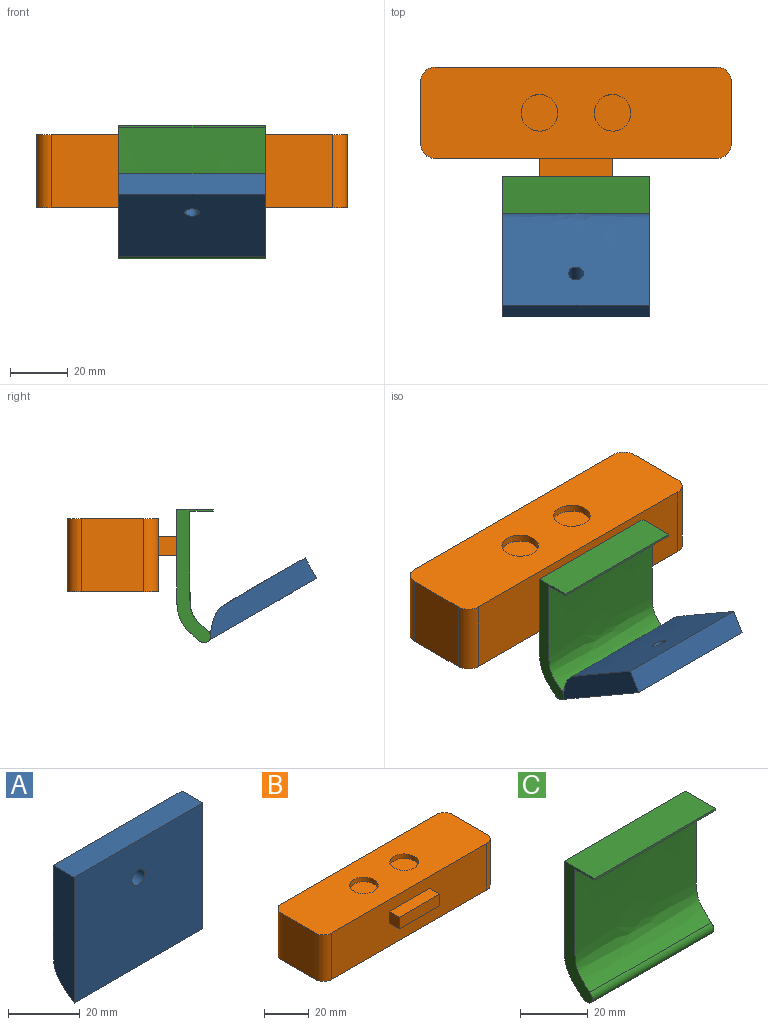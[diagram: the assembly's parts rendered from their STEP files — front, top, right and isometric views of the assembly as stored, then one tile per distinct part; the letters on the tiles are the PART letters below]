
ASSEMBLY  parts=3 mates=2
PART A: 6 faces, bbox 50.8x8.3x43 mm
  f0: extruded ~50.8x42.97mm, area 2327.7mm2, adj f1,f2,f3,f4,f5
  f1: plane 50.8x8.18mm, normal (0,0,1), area 415.3mm2, adj f0,f2,f3,f4
  f2: plane 50.8x42.97mm, normal (0,-1,0), area 2162.3mm2, adj f0,f1,f3,f4,f5
  f3: plane 42.97x8.26mm, normal (1,0,0), area 321.8mm2, adj f0,f1,f2
  f4: plane 42.97x8.26mm, normal (-1,0,0), area 321.8mm2, adj f0,f1,f2
  f5: cylinder r=2.55mm len=8.21mm, axis (0,-1,0), area 131.7mm2, adj f0,f2
PART B: 19 faces, bbox 108x38.1x25.4 mm
  f0: cylinder r=6.35mm len=12.7mm, axis (0,0,-1), area 101.3mm2, adj f6,f18
  f1: cylinder r=6.35mm len=12.7mm, axis (0,0,-1), area 101.3mm2, adj f6,f17
  f2: plane 97.79x25.4mm, normal (0,-1,0), area 2322.6mm2, adj f6,f7,f8,f11,f12,f13,f14,f15
  f3: plane 25.4x21.59mm, normal (1,0,0), area 548.4mm2, adj f6,f7,f8,f9
  f4: plane 97.79x25.4mm, normal (0,1,0), area 2483.9mm2, adj f6,f7,f9,f10
  f5: plane 25.4x21.59mm, normal (-1,0,0), area 548.4mm2, adj f6,f7,f10,f11
  f6: plane 107.95x31.75mm, normal (0,0,1), area 3151.9mm2, adj f0,f1,f2,f3,f4,f5,f8,f9
  f7: plane 107.95x31.75mm, normal (0,0,-1), area 3405.3mm2, adj f2,f3,f4,f5,f8,f9,f10,f11
  f8: cylinder r=5.08mm len=25.4mm, axis (0,0,1), area 202.7mm2, adj f2,f3,f6,f7
  f9: cylinder r=5.08mm len=25.4mm, axis (0,0,-1), area 202.7mm2, adj f3,f4,f6,f7
  f10: cylinder r=5.08mm len=25.4mm, axis (0,0,1), area 202.7mm2, adj f4,f5,f6,f7
  f11: cylinder r=5.08mm len=25.4mm, axis (0,0,-1), area 202.7mm2, adj f2,f5,f6,f7
  f12: plane 25.4x6.35mm, normal (0,0,1), area 161.3mm2, adj f2,f13,f15,f16
  f13: plane 6.35x6.35mm, normal (-1,0,0), area 40.3mm2, adj f2,f12,f14,f16
  f14: plane 25.4x6.35mm, normal (0,0,-1), area 161.3mm2, adj f2,f13,f15,f16
  f15: plane 6.35x6.35mm, normal (1,0,0), area 40.3mm2, adj f2,f12,f14,f16
  f16: plane 25.4x6.35mm, normal (0,-1,0), area 161.3mm2, adj f12,f13,f14,f15
  f17: plane 12.7x12.7mm, normal (0,0,1), area 126.7mm2, adj f1
  f18: plane 12.7x12.7mm, normal (0,0,1), area 126.7mm2, adj f0
PART C: 10 faces, bbox 50.8x12.7x46.3 mm
  f0: plane 46.29x12.7mm, normal (1,0,0), area 225mm2, adj f1,f3,f4,f5,f6,f7,f8,f9
  f1: plane 50.8x0.67mm, normal (0,-1,0), area 34.1mm2, adj f0,f2,f4,f6
  f2: plane 46.29x12.7mm, normal (-1,0,0), area 225mm2, adj f1,f3,f4,f5,f6,f7,f8,f9
  f3: plane 50.8x32.22mm, normal (0,1,0), area 1636.7mm2, adj f0,f2,f4,f5
  f4: plane 50.8x12.7mm, normal (0,0,1), area 645.2mm2, adj f0,f1,f2,f3
  f5: extruded ~50.8x13.53mm, area 832.4mm2, adj f0,f2,f3,f9
  f6: plane 50.8x8.18mm, normal (0,0,-1), area 415.3mm2, adj f0,f1,f2,f7
  f7: extruded ~50.8x41.49mm, area 2225.3mm2, adj f0,f2,f6,f8
  f8: cylinder r=2.54mm len=50.8mm, axis (1,0,0), area 183.5mm2, adj f0,f2,f7,f9
  f9: cylinder r=2.54mm len=50.8mm, axis (1,0,0), area 196.1mm2, adj f0,f2,f5,f8
PLACE A rot(axis=(1,0,0),60deg) t=(-29.97,-52.86,-15.7)mm
PLACE B rot(axis=(0.05,0.65,-0.75),0deg) t=(-29.97,-20.87,-38.33)mm
PLACE C rot(axis=(0.05,0.65,-0.75),0deg) t=(-29.97,-20.87,-35.16)mm
MATE fastened C.f3 <-> B.f16  axis (0,1,0) through (-29.97,-43.09,-9.76)mm
MATE revolute A.f3 <-> C.f0  axis (1,0,0) through (-4.57,-54.52,-55.18)mm
